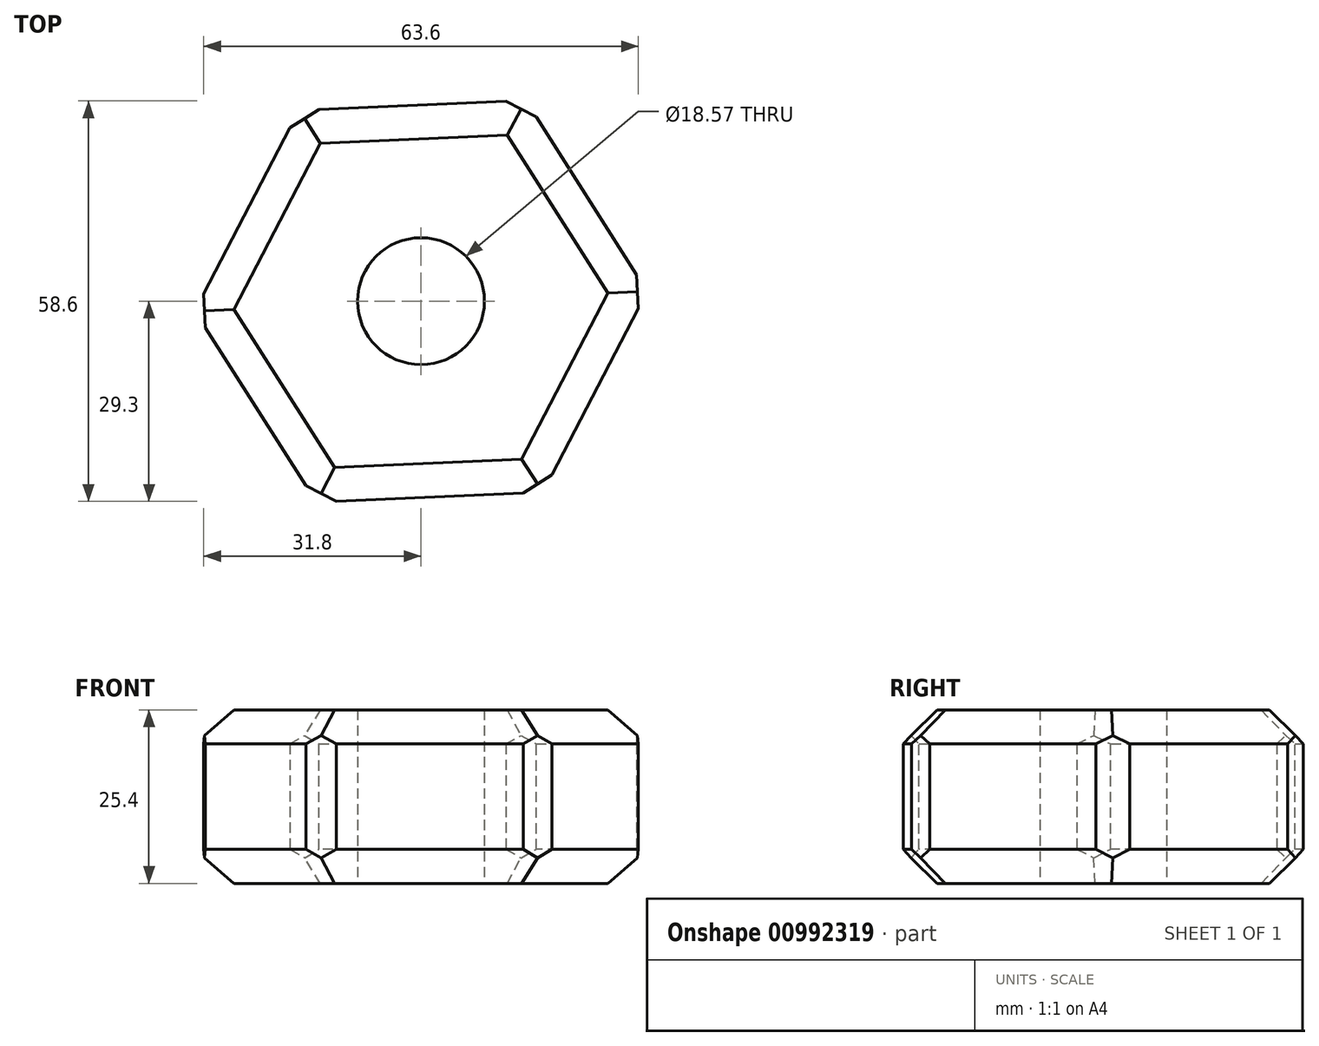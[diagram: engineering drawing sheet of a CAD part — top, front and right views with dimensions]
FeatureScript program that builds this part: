
annotation { "Feature Type Name" : "Feature", "Feature Type Description" : "" }
export const myFeature = defineFeature(function(context is Context, id is Id, definition is map)
    precondition{}
    {
        {
            var Q0;
            Q0=qCreatedBy(makeId("Top.planeOp"),FACE);
            var sketch = newSketch(context, id + "F0", { "sketchPlane" : qUnion([Q0])});
            skCircle(sketch, "E0.cCircle", {"center": v(0, 0) * mm, "radius": 28.72 * mm, "construction": true});
            skLineSegment(sketch, "E0.0", {"start": v(-33.13, -1.46) * mm, "end": v(-17.83, 27.96) * mm});
            skLineSegment(sketch, "E0.1", {"start": v(-17.83, 27.96) * mm, "end": v(15.3, 29.42) * mm});
            skLineSegment(sketch, "E0.2", {"start": v(15.3, 29.42) * mm, "end": v(33.13, 1.46) * mm});
            skLineSegment(sketch, "E0.3", {"start": v(33.13, 1.46) * mm, "end": v(17.83, -27.96) * mm});
            skLineSegment(sketch, "E0.4", {"start": v(17.83, -27.96) * mm, "end": v(-15.3, -29.42) * mm});
            skLineSegment(sketch, "E0.5", {"start": v(-15.3, -29.42) * mm, "end": v(-33.13, -1.46) * mm});
            skPoint(sketch, "E0.0.midPoint", {"position": v(-25.48, 13.25) * mm});
            skCircle(sketch, "E1", {"center": v(0, 0) * mm, "radius": 9.28 * mm});
            skSolve(sketch);
        }
        {
            var Q0;
            Q0=makeQuery(id+"F0.imprint","IMPRINT",FACE,{"disambiguationData":[TD([[makeQuery(id+"F0.imprint","IMPRINT",EDGE,{"derivedFrom":sQuery(id+"F0.wireOp",EDGE,"E0.0")}),-1.0]])]});
            extrude(context, id + "F1", {"entities" : qUnion([Q0]), "depth" : 25.4 * mm, "offsetDistance" : 25.4 * mm});
        }
        {
            var Q0;
            Q0=makeQuery(id+"F1.opExtrude","SWEPT_EDGE",EDGE,{"disambiguationData":[OSD([sQuery(id+"F0.wireOp",EDGE,"E0.0"),sQuery(id+"F0.wireOp",EDGE,"E0.1")])]});
            var Q1;
            Q1=makeQuery(id+"F1.opExtrude","SWEPT_EDGE",EDGE,{"disambiguationData":[OSD([sQuery(id+"F0.wireOp",EDGE,"E0.1"),sQuery(id+"F0.wireOp",EDGE,"E0.2")])]});
            var Q2;
            Q2=makeQuery(id+"F1.opExtrude","SWEPT_EDGE",EDGE,{"disambiguationData":[OSD([sQuery(id+"F0.wireOp",EDGE,"E0.2"),sQuery(id+"F0.wireOp",EDGE,"E0.3")])]});
            var Q3;
            Q3=makeQuery(id+"F1.opExtrude","SWEPT_EDGE",EDGE,{"disambiguationData":[OSD([sQuery(id+"F0.wireOp",EDGE,"E0.0"),sQuery(id+"F0.wireOp",EDGE,"E0.5")])]});
            var Q4;
            Q4=makeQuery(id+"F1.opExtrude","SWEPT_EDGE",EDGE,{"disambiguationData":[OSD([sQuery(id+"F0.wireOp",EDGE,"E0.4"),sQuery(id+"F0.wireOp",EDGE,"E0.5")])]});
            var Q5;
            Q5=makeQuery(id+"F1.opExtrude","SWEPT_EDGE",EDGE,{"disambiguationData":[OSD([sQuery(id+"F0.wireOp",EDGE,"E0.3"),sQuery(id+"F0.wireOp",EDGE,"E0.4")])]});
            chamfer(context, id + "F2", {"entities" : qUnion([Q0, Q1, Q2, Q3, Q4, Q5]), "width" : 5 * mm, "tangentPropagation" : true});
        }
        {
            var Q0;
            Q0=makeQuery(id+"F1.opExtrude","CAP_EDGE",EDGE,{"disambiguationData":[OSD([sQuery(id+"F0.wireOp",EDGE,"E0.2")])],"isStart":true});
            var Q1;
            Q1=makeQuery(id+"F1.opExtrude","CAP_EDGE",EDGE,{"disambiguationData":[OSD([sQuery(id+"F0.wireOp",EDGE,"E0.1")])],"isStart":true});
            var Q2;
            Q2=makeQuery(id+"F1.opExtrude","CAP_EDGE",EDGE,{"disambiguationData":[OSD([sQuery(id+"F0.wireOp",EDGE,"E0.2")])],"isStart":false});
            var Q3;
            Q3=makeQuery(id+"F1.opExtrude","CAP_EDGE",EDGE,{"disambiguationData":[OSD([sQuery(id+"F0.wireOp",EDGE,"E0.1")])],"isStart":false});
            var Q4;
            Q4=makeQuery(id+"F1.opExtrude","CAP_EDGE",EDGE,{"disambiguationData":[OSD([sQuery(id+"F0.wireOp",EDGE,"E0.0")])],"isStart":false});
            var Q5;
            Q5=makeQuery(id+"F1.opExtrude","CAP_EDGE",EDGE,{"disambiguationData":[OSD([sQuery(id+"F0.wireOp",EDGE,"E0.0")])],"isStart":true});
            var Q6;
            Q6=makeQuery(id+"F1.opExtrude","CAP_EDGE",EDGE,{"disambiguationData":[OSD([sQuery(id+"F0.wireOp",EDGE,"E0.5")])],"isStart":false});
            var Q7;
            Q7=makeQuery(id+"F1.opExtrude","CAP_EDGE",EDGE,{"disambiguationData":[OSD([sQuery(id+"F0.wireOp",EDGE,"E0.5")])],"isStart":true});
            var Q8;
            Q8=makeQuery(id+"F1.opExtrude","CAP_EDGE",EDGE,{"disambiguationData":[OSD([sQuery(id+"F0.wireOp",EDGE,"E0.3")])],"isStart":false});
            var Q9;
            Q9=makeQuery(id+"F1.opExtrude","CAP_EDGE",EDGE,{"disambiguationData":[OSD([sQuery(id+"F0.wireOp",EDGE,"E0.3")])],"isStart":true});
            var Q10;
            Q10=makeQuery(id+"F1.opExtrude","CAP_EDGE",EDGE,{"disambiguationData":[OSD([sQuery(id+"F0.wireOp",EDGE,"E0.4")])],"isStart":true});
            var Q11;
            Q11=makeQuery(id+"F1.opExtrude","CAP_EDGE",EDGE,{"disambiguationData":[OSD([sQuery(id+"F0.wireOp",EDGE,"E0.4")])],"isStart":false});
            chamfer(context, id + "F3", {"entities" : qUnion([Q0, Q1, Q2, Q3, Q4, Q5, Q6, Q7, Q8, Q9, Q10, Q11]), "width" : 5 * mm, "tangentPropagation" : true});
        }
    });
